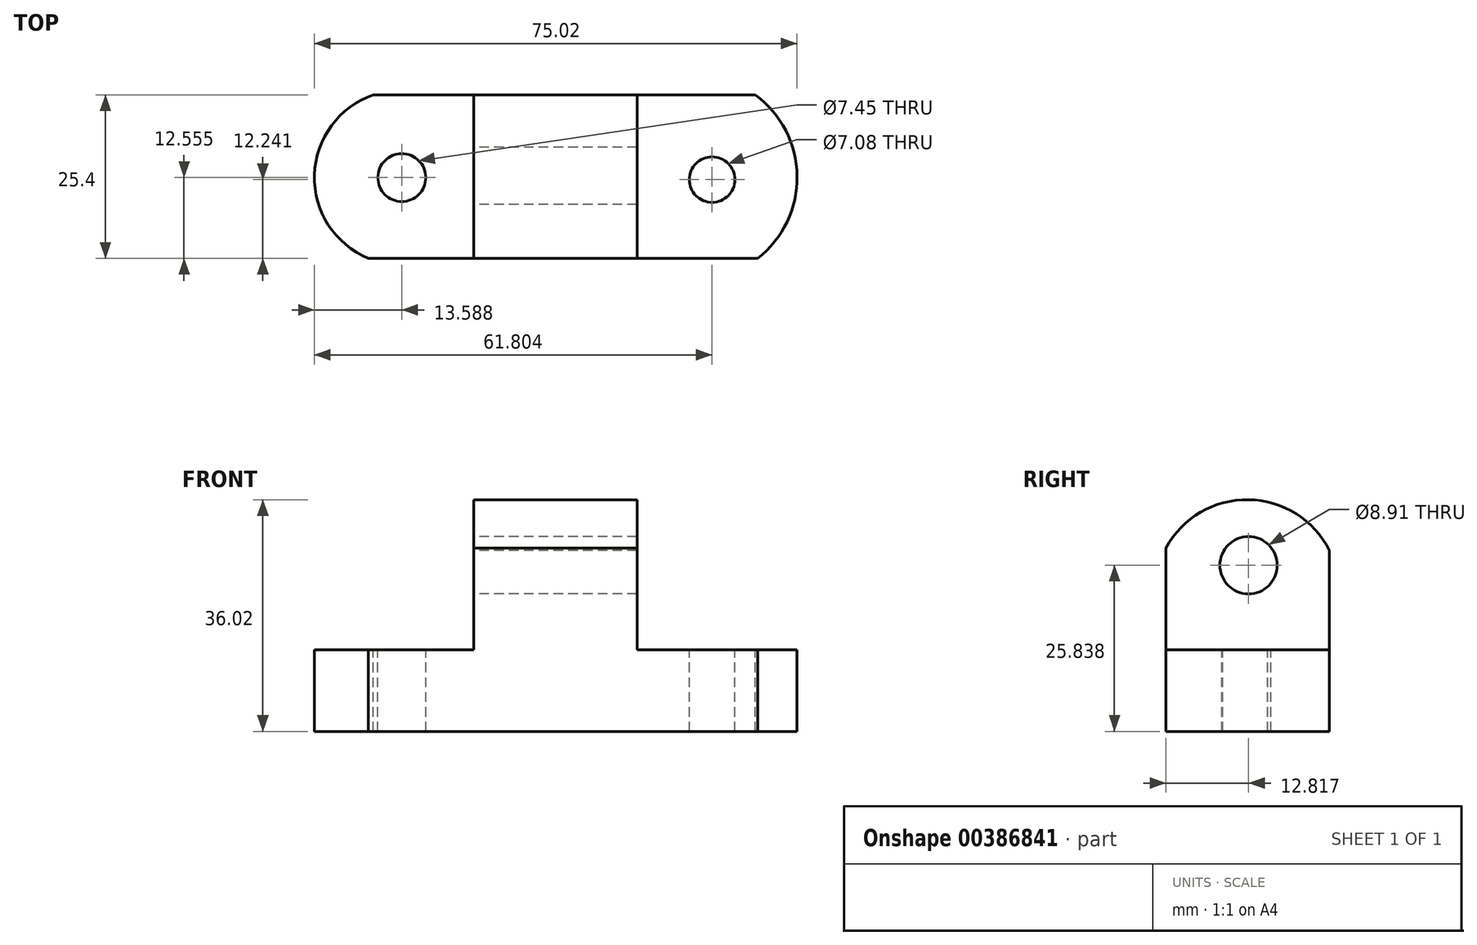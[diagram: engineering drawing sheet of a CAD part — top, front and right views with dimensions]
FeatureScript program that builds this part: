
annotation { "Feature Type Name" : "Feature", "Feature Type Description" : "" }
export const myFeature = defineFeature(function(context is Context, id is Id, definition is map)
    precondition{}
    {
        {
            var Q0;
            Q0=qCreatedBy(makeId("Front.planeOp"),FACE);
            var sketch = newSketch(context, id + "F0", { "sketchPlane" : qUnion([Q0])});
            skLineSegment(sketch, "E0", {"start": v(-32.4, 0) * mm, "end": v(-32.4, 12.7) * mm});
            skLineSegment(sketch, "E1", {"start": v(-32.4, 12.7) * mm, "end": v(-7, 12.7) * mm});
            skLineSegment(sketch, "E2", {"start": v(-7, 12.7) * mm, "end": v(-7, 36.49) * mm});
            skLineSegment(sketch, "E3", {"start": v(-7, 36.49) * mm, "end": v(18.4, 36.49) * mm});
            skLineSegment(sketch, "E4", {"start": v(18.4, 36.49) * mm, "end": v(18.4, 12.7) * mm});
            skLineSegment(sketch, "E5", {"start": v(18.4, 12.7) * mm, "end": v(43.8, 12.7) * mm});
            skLineSegment(sketch, "E6", {"start": v(43.8, 12.7) * mm, "end": v(43.8, 0) * mm});
            skLineSegment(sketch, "E7", {"start": v(43.8, 0) * mm, "end": v(-32.4, 0) * mm});
            skSolve(sketch);
        }
        {
            var Q0;
            Q0 = qSketchRegion(id + "F0", true);
            extrude(context, id + "F1", {"entities" : qUnion([Q0]), "depth" : 25.4 * mm});
        }
        {
            var Q0;
            Q0=makeQuery(id+"F1.opExtrude","SWEPT_FACE",FACE,{"disambiguationData":[OSD([sQuery(id+"F0.wireOp",EDGE,"E2")])]});
            var sketch = newSketch(context, id + "F2", { "sketchPlane" : qUnion([Q0])});
            skArc(sketch, "E8", {"start": v(25.4, 28.53) * mm, "mid": v(12.58, 36.02) * mm, "end": v(0, 28.14) * mm});
            skSolve(sketch);
        }
        {
            var Q0;
            {var subQ0=sQuery(id+"F2.wireOp",EDGE,"E8");Q0=makeQuery(id+"F2.imprint","IMPRINT",FACE,{"disambiguationData":[TD([[makeQuery(id+"F2.imprint","IMPRINT",EDGE,{"derivedFrom":subQ0}),-1.0]])]});}
            extrude(context, id + "F3", {"entities" : qUnion([Q0]), "operationType" : NewBodyOperationType.REMOVE, "oppositeDirection" : true, "depth" : 25.4 * mm});
        }
        {
            var Q0;
            Q0=makeQuery(id+"F1.opExtrude","SWEPT_FACE",FACE,{"disambiguationData":[OSD([sQuery(id+"F0.wireOp",EDGE,"E1")])]});
            var sketch = newSketch(context, id + "F4", { "sketchPlane" : qUnion([Q0])});
            skArc(sketch, "E9", {"start": v(-22.57, 0) * mm, "mid": v(-31.73, -12.43) * mm, "end": v(-23.34, -25.4) * mm});
            skArc(sketch, "E10", {"start": v(35.44, -25.4) * mm, "mid": v(43.46, -12.51) * mm, "end": v(34.87, 0) * mm});
            skSolve(sketch);
        }
        {
            var Q0;
            {var subQ0=sQuery(id+"F4.wireOp",EDGE,"E9");Q0=makeQuery(id+"F4.imprint","IMPRINT",FACE,{"disambiguationData":[TD([[makeQuery(id+"F4.imprint","IMPRINT",EDGE,{"derivedFrom":subQ0}),-1.0]])]});}
            extrude(context, id + "F5", {"entities" : qUnion([Q0]), "operationType" : NewBodyOperationType.REMOVE, "oppositeDirection" : true, "depth" : 25.4 * mm});
        }
        {
            var Q0;
            Q0=makeQuery(id+"F1.opExtrude","SWEPT_FACE",FACE,{"disambiguationData":[OSD([sQuery(id+"F0.wireOp",EDGE,"E5")])]});
            var sketch = newSketch(context, id + "F6", { "sketchPlane" : qUnion([Q0])});
            skArc(sketch, "E11", {"start": v(37.17, -25.4) * mm, "mid": v(43.28, -12.6) * mm, "end": v(36.79, 0) * mm});
            skSolve(sketch);
        }
        {
            var Q0;
            {var subQ0=sQuery(id+"F6.wireOp",EDGE,"E11");Q0=makeQuery(id+"F6.imprint","IMPRINT",FACE,{"disambiguationData":[TD([[makeQuery(id+"F6.imprint","IMPRINT",EDGE,{"derivedFrom":subQ0}),-1.0]])]});}
            extrude(context, id + "F7", {"entities" : qUnion([Q0]), "operationType" : NewBodyOperationType.REMOVE, "oppositeDirection" : true, "depth" : 25.4 * mm});
        }
        {
            var Q0;
            Q0=makeQuery(id+"F1.opExtrude","SWEPT_FACE",FACE,{"disambiguationData":[OSD([sQuery(id+"F0.wireOp",EDGE,"E1")])]});
            var sketch = newSketch(context, id + "F8", { "sketchPlane" : qUnion([Q0])});
            skCircle(sketch, "E12", {"center": v(-18.15, -12.85) * mm, "radius": 3.73 * mm});
            skCircle(sketch, "E13", {"center": v(30.06, -13.16) * mm, "radius": 3.54 * mm});
            skSolve(sketch);
        }
        {
            var Q0;
            Q0 = qSketchRegion(id + "F8", true);
            extrude(context, id + "F9", {"entities" : qUnion([Q0]), "operationType" : NewBodyOperationType.REMOVE, "oppositeDirection" : true, "depth" : 25.4 * mm});
        }
        {
            var Q0;
            Q0=makeQuery(id+"F1.opExtrude","SWEPT_FACE",FACE,{"disambiguationData":[OSD([sQuery(id+"F0.wireOp",EDGE,"E2")])]});
            var sketch = newSketch(context, id + "F10", { "sketchPlane" : qUnion([Q0])});
            skCircle(sketch, "E14", {"center": v(12.58, 25.84) * mm, "radius": 4.46 * mm});
            skSolve(sketch);
        }
        {
            var Q0;
            Q0 = qSketchRegion(id + "F10", true);
            extrude(context, id + "F11", {"entities" : qUnion([Q0]), "operationType" : NewBodyOperationType.REMOVE, "oppositeDirection" : true, "depth" : 25.4 * mm});
        }
    });
